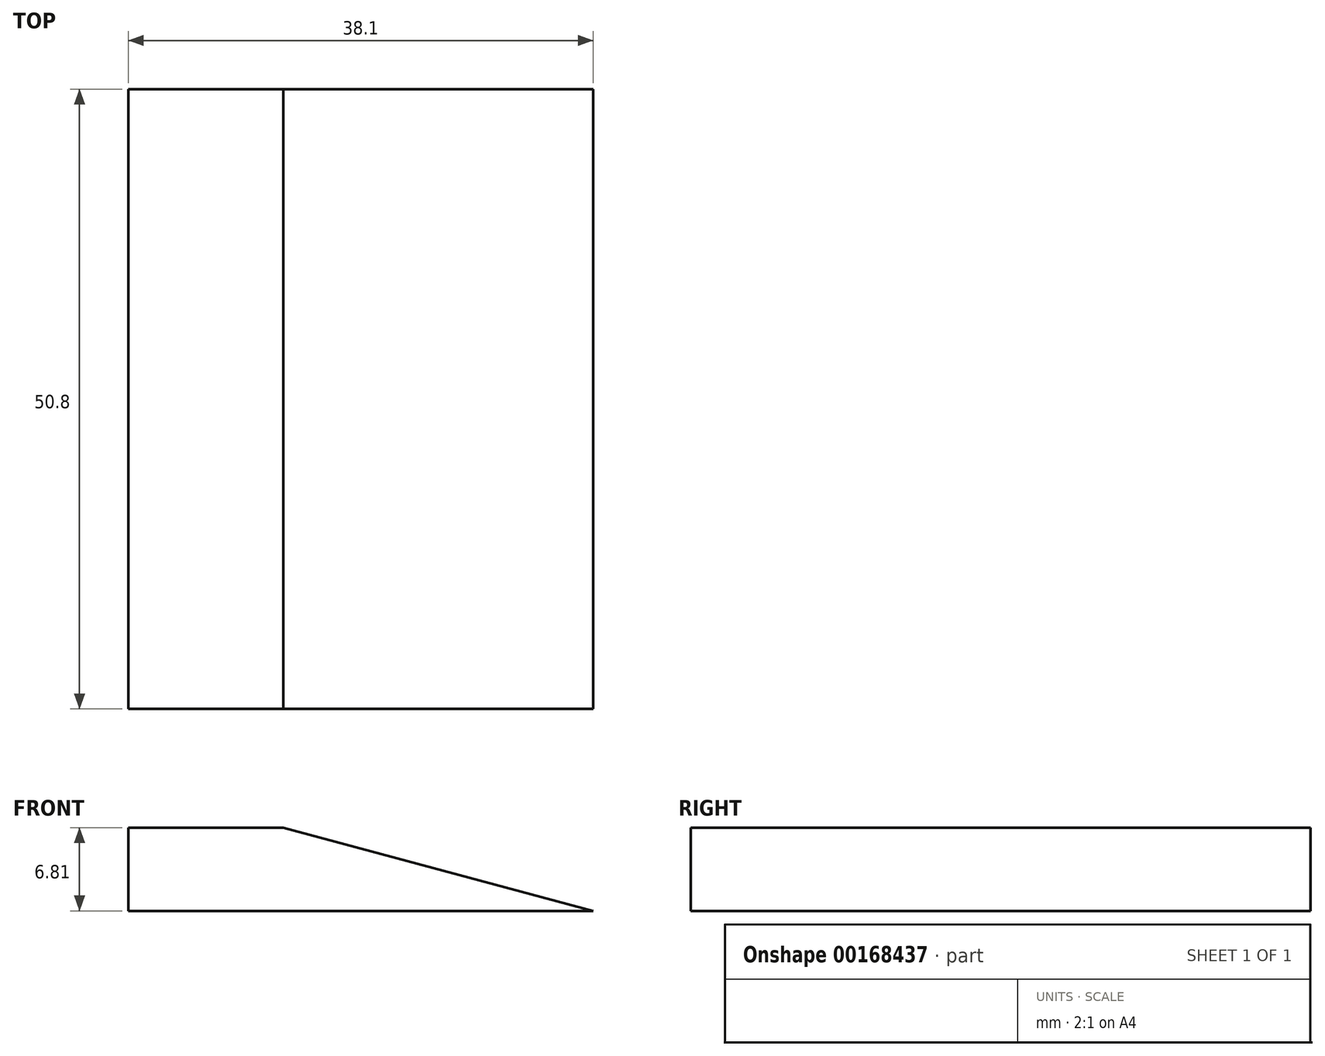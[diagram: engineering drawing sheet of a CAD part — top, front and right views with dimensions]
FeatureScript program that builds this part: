
annotation { "Feature Type Name" : "Feature", "Feature Type Description" : "" }
export const myFeature = defineFeature(function(context is Context, id is Id, definition is map)
    precondition{}
    {
        {
            var Q0;
            Q0=qCreatedBy(makeId("Front.planeOp"),FACE);
            var sketch = newSketch(context, id + "F0", { "sketchPlane" : qUnion([Q0])});
            skLineSegment(sketch, "E0", {"start": v(0, 0) * mm, "end": v(25.4, 0) * mm});
            skLineSegment(sketch, "E1", {"start": v(25.4, 0) * mm, "end": v(0, 6.8) * mm});
            skLineSegment(sketch, "E2", {"start": v(0, 6.8) * mm, "end": v(0, 0) * mm});
            skSolve(sketch);
        }
        {
            var Q0;
            Q0=makeQuery(id+"F0.imprint","IMPRINT",FACE,{"disambiguationData":[TD([[makeQuery(id+"F0.imprint","IMPRINT",EDGE,{"derivedFrom":sQuery(id+"F0.wireOp",EDGE,"E0")}),1.0]])]});
            extrude(context, id + "F1", {"entities" : qUnion([Q0]), "depth" : 50.8 * mm});
        }
        {
            var Q0;
            Q0=makeQuery(id+"F1.opExtrude","SWEPT_FACE",FACE,{"disambiguationData":[OSD([sQuery(id+"F0.wireOp",EDGE,"E2")])]});
            extrude(context, id + "F2", {"entities" : qUnion([Q0]), "operationType" : NewBodyOperationType.ADD, "depth" : 12.7 * mm});
        }
    });
